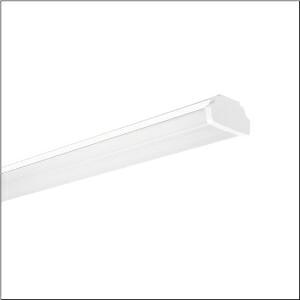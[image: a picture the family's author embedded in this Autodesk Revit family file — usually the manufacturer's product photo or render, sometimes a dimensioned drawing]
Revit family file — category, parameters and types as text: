
# Revit family: modario_r__31_ho_53bm811d2v4120_c329
name_source: partatom
category: Lighting Fixtures
units: mm (PartAtom-declared; Revit-internal decimal feet)

## family parameters
Cut with Voids When Loaded = No
Host = Face
Light Source = No
Part Type = Normal
Room Calculation Point = No
Round Connector Dimension = Use Diameter
Shared = No

## types (1)
- --- (1 x LED, 12350 lm, 79.5 W, 4000K)
    Apparent Load = 80 VA
    CIE Flux Codes = 52 78 94 90 100
    Color Rendering = 80
    Color Temperature = 4000K
    Default Elevation = 1800 mm
    Description = Modario® 31 HO, luminaire insert, of sheet steel, coil coated, white, length: 1.495mm, width: 81mm, height: 82mm, 5x system unit, system units: 299mm, LED rated luminous flux: 12.350lm, light colour: 840, control gear: DALI 2, control gear: ECG DALI, with plug, 5-pole, with phase selection, mains connection: 220..240V, AC, 50/60Hz, rated input power: 79W, through-wiring accessed according to module size, primary optical cover: cover, of PMMA, light emission: direct distribution, primary light characteristic: symmetric, protection rating (complete): IP20, protection rating (LED compartment): IP50, insulation class (complete): insulation class I (protective earthing), certification: CE, ENEC, VDE, UKCA, impact resistance: IK03, permissible ambient temperature for indoor applications: -25..+30°C, corresponds to IFS (International Featured Standards) requirements for safety and quality in the food industry, reducing of maximum allowable ambient temperature of 5°C with ceiling mounting, packaging unit: 1 piece
    Height = 92 mm
    Lamp = 1 x LED
    Lamp Light Flux = 12350 lm
    Lamp Power = 79.5 W
    Lamp count = 1
    Length = 1495 mm
    Luminous efficacy = 155 lm/W
    Manufacturer = Siteco
    ModVariant = No
    Model = 53BM811D2V4120
    Mounting Place = Ceiling
    Mounting Type = Pendant
    Number of Poles = 1
    OnlyDefault = Yes
    Power Factor = 1
    Product Name = Modario® 31 HO
    Product group = luminaire insert
    ProductGroupID = 901
    Protection Class = Protection class I
    Protection Degree = IP 20
    RLX_Detail_Level = 1
    RLX_Emergency_Light_Flux = 0 lm
    RLX_Emergency_Type = 0
    RLX_Emergency_Type_DB = No
    RlxData = <blob elided: 42241 chars, md5=78a95108>
    Socket = socket
    Standby Power = 0 W
    System Light Flux = 12350 lm
    System Power = 80 W
    Type Comments = factory setting: luminous flux: 100 % | dim-lin: 254 | 345 mA
    Type Image = l_1300283.jpg
    URL = http://relux.com
    VarID = @adj_152711
    Voltage = 0 V
    Weight = 0.00 kg
    Width = 81 mm

## geometry (parser evidence)
native form markers: Blend x4, Sweep x12
no freeform markers — native parametric forms only
